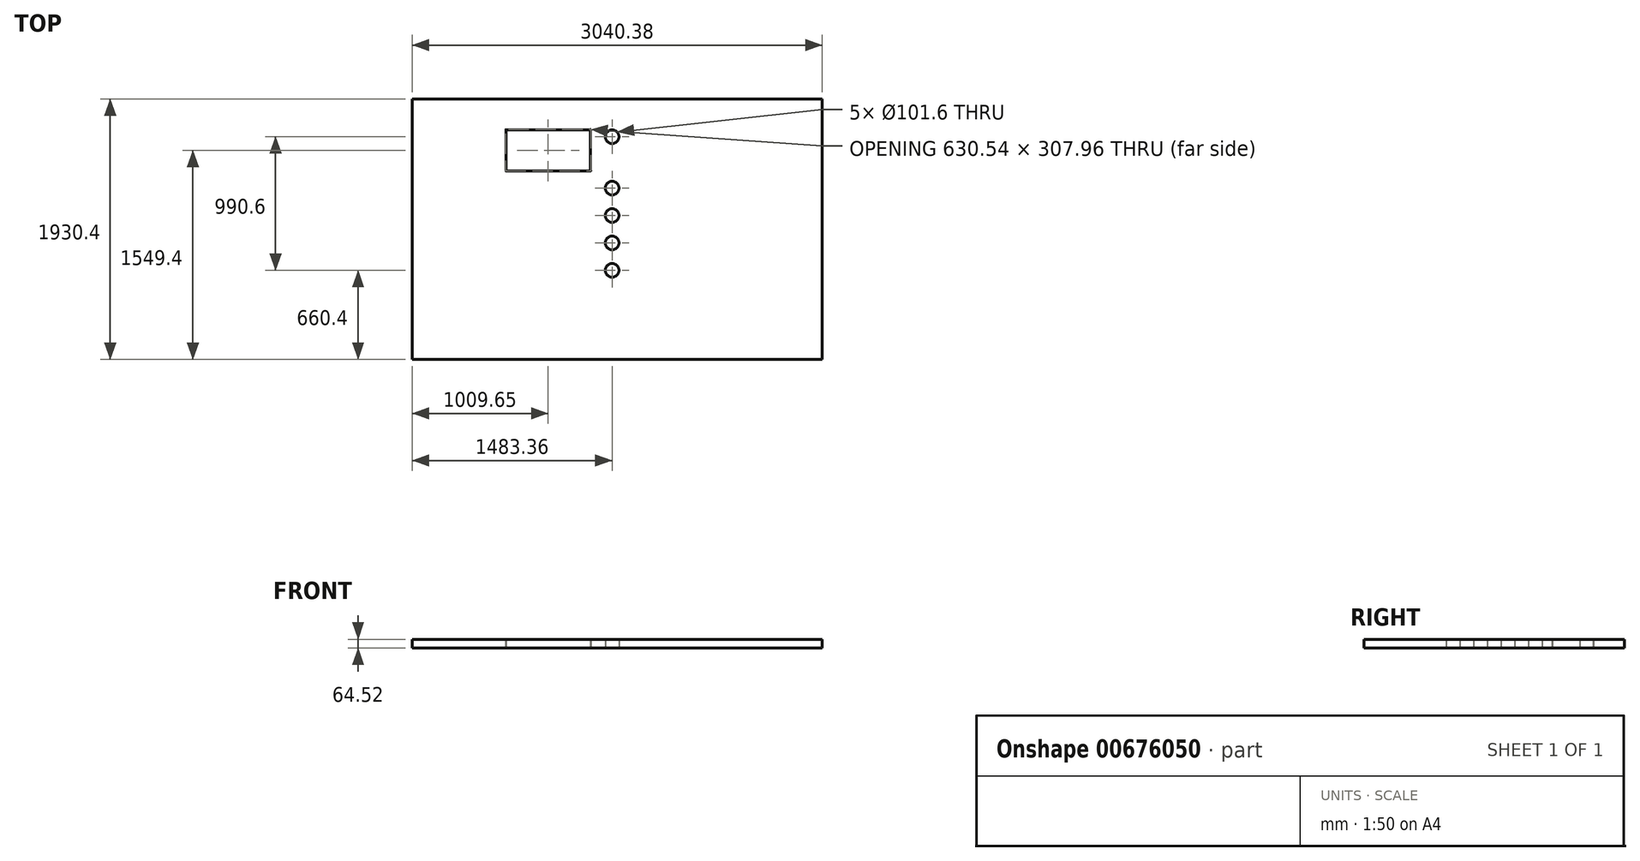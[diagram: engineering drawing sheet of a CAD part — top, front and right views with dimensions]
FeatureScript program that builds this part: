
annotation { "Feature Type Name" : "Feature", "Feature Type Description" : "" }
export const myFeature = defineFeature(function(context is Context, id is Id, definition is map)
    precondition{}
    {
        {
            var Q0;
            Q0=qCreatedBy(makeId("Top.planeOp"),FACE);
            var sketch = newSketch(context, id + "F0", { "sketchPlane" : qUnion([Q0])});
            skLineSegment(sketch, "E0", {"start": v(-1520.2, -965.2) * mm, "end": v(1520.19, -965.2) * mm});
            skLineSegment(sketch, "E1", {"start": v(1520.19, -965.2) * mm, "end": v(1520.19, 965.2) * mm});
            skLineSegment(sketch, "E2", {"start": v(1520.19, 965.2) * mm, "end": v(-1520.19, 965.2) * mm});
            skLineSegment(sketch, "E3", {"start": v(-1520.2, 965.2) * mm, "end": v(-1520.2, -965.2) * mm});
            skLineSegment(sketch, "E4", {"start": v(-824.23, 431.8) * mm, "end": v(-824.23, 736.6) * mm});
            skArc(sketch, "E5", {"start": v(-822.62, 736.6) * mm, "mid": v(-824.23, 738.21) * mm, "end": v(-825.84, 736.6) * mm});
            skArc(sketch, "E6", {"start": v(-825.84, 431.8) * mm, "mid": v(-824.23, 430.19) * mm, "end": v(-822.62, 431.8) * mm});
            skLineSegment(sketch, "E7", {"start": v(-196.85, 431.8) * mm, "end": v(-196.85, 736.6) * mm});
            skArc(sketch, "E8", {"start": v(-195.24, 736.6) * mm, "mid": v(-196.85, 738.21) * mm, "end": v(-198.46, 736.6) * mm});
            skArc(sketch, "E9", {"start": v(-198.46, 431.8) * mm, "mid": v(-196.85, 430.19) * mm, "end": v(-195.24, 431.8) * mm});
            skLineSegment(sketch, "E10", {"start": v(-824.23, 431.8) * mm, "end": v(-196.85, 431.8) * mm});
            skArc(sketch, "E11", {"start": v(-196.85, 430.19) * mm, "mid": v(-195.24, 431.8) * mm, "end": v(-196.85, 433.41) * mm});
            skArc(sketch, "E12", {"start": v(-824.23, 433.41) * mm, "mid": v(-825.84, 431.8) * mm, "end": v(-824.23, 430.19) * mm});
            skLineSegment(sketch, "E13", {"start": v(-824.23, 736.6) * mm, "end": v(-196.85, 736.6) * mm});
            skArc(sketch, "E14", {"start": v(-196.85, 734.99) * mm, "mid": v(-195.24, 736.6) * mm, "end": v(-196.85, 738.21) * mm});
            skArc(sketch, "E15", {"start": v(-824.23, 738.21) * mm, "mid": v(-825.84, 736.6) * mm, "end": v(-824.23, 734.99) * mm});
            skArc(sketch, "E16", {"start": v(-36.83, 635) * mm, "mid": v(13.97, 685.8) * mm, "end": v(-36.83, 736.6) * mm});
            skArc(sketch, "E17", {"start": v(-36.83, 736.6) * mm, "mid": v(-87.63, 685.8) * mm, "end": v(-36.83, 635) * mm});
            skArc(sketch, "E18", {"start": v(-36.83, 254) * mm, "mid": v(13.97, 304.8) * mm, "end": v(-36.83, 355.6) * mm});
            skArc(sketch, "E19", {"start": v(-36.83, 355.6) * mm, "mid": v(-87.63, 304.8) * mm, "end": v(-36.83, 254) * mm});
            skArc(sketch, "E20", {"start": v(-36.83, 50.8) * mm, "mid": v(13.97, 101.6) * mm, "end": v(-36.83, 152.4) * mm});
            skArc(sketch, "E21", {"start": v(-36.83, 152.4) * mm, "mid": v(-87.63, 101.6) * mm, "end": v(-36.83, 50.8) * mm});
            skArc(sketch, "E22", {"start": v(-36.83, -152.4) * mm, "mid": v(13.97, -101.6) * mm, "end": v(-36.83, -50.8) * mm});
            skArc(sketch, "E23", {"start": v(-36.83, -50.8) * mm, "mid": v(-87.63, -101.6) * mm, "end": v(-36.83, -152.4) * mm});
            skArc(sketch, "E24", {"start": v(-36.83, -355.6) * mm, "mid": v(13.97, -304.8) * mm, "end": v(-36.83, -254) * mm});
            skArc(sketch, "E25", {"start": v(-36.83, -254) * mm, "mid": v(-87.63, -304.8) * mm, "end": v(-36.83, -355.6) * mm});
            skSolve(sketch);
        }
        {
            var Q0;
            Q0 = qSketchRegion(id + "F0", true);
            extrude(context, id + "F1", {"entities" : qUnion([Q0]), "depth" : 64.52 * mm, "offsetDistance" : 25.4 * mm});
        }
    });
